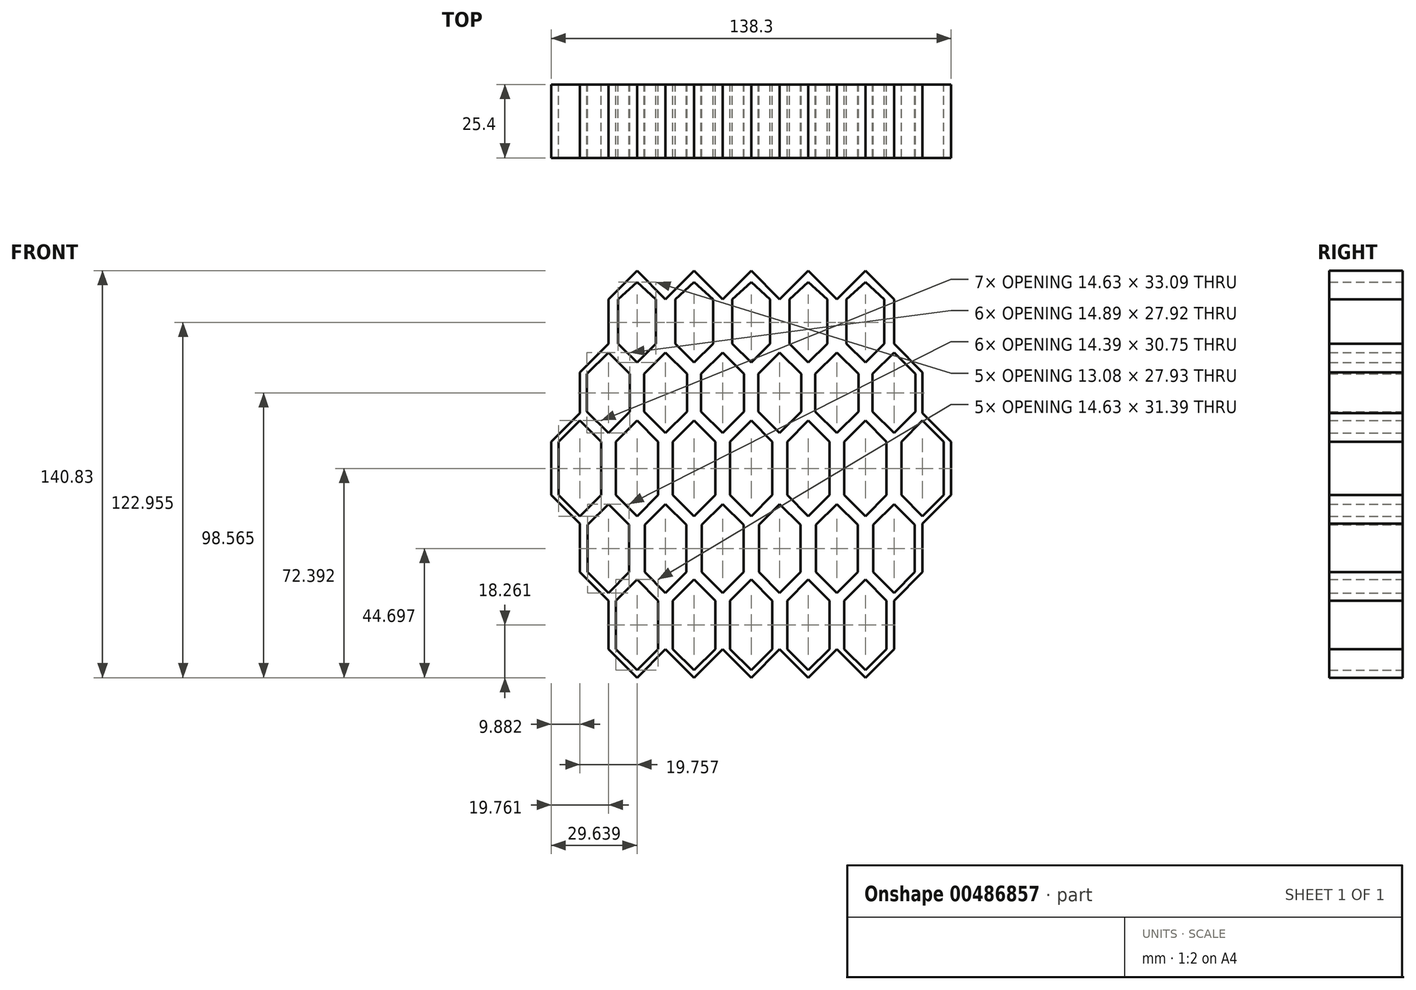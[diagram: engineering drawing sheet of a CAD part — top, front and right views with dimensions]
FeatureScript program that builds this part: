
annotation { "Feature Type Name" : "Feature", "Feature Type Description" : "" }
export const myFeature = defineFeature(function(context is Context, id is Id, definition is map)
    precondition{}
    {
        {
            var Q0;
            Q0=qCreatedBy(makeId("Front.planeOp"),FACE);
            var sketch = newSketch(context, id + "F0", { "sketchPlane" : qUnion([Q0])});
            skLineSegment(sketch, "E0", {"start": v(-42.67, 59.2) * mm, "end": v(-52.55, 49.33) * mm});
            skLineSegment(sketch, "E1", {"start": v(-52.55, 49.33) * mm, "end": v(-52.55, 33.9) * mm});
            skLineSegment(sketch, "E2", {"start": v(-52.55, 33.9) * mm, "end": v(-42.67, 24.03) * mm});
            skLineSegment(sketch, "E3", {"start": v(-42.67, 24.03) * mm, "end": v(-32.8, 33.9) * mm});
            skLineSegment(sketch, "E4", {"start": v(-32.8, 33.9) * mm, "end": v(-32.8, 49.33) * mm});
            skLineSegment(sketch, "E5", {"start": v(-32.8, 49.33) * mm, "end": v(-42.67, 59.2) * mm});
            skLineSegment(sketch, "E6", {"start": v(-32.8, 49.33) * mm, "end": v(-22.91, 59.2) * mm});
            skLineSegment(sketch, "E7", {"start": v(-22.91, 59.2) * mm, "end": v(-13.04, 49.33) * mm});
            skLineSegment(sketch, "E8", {"start": v(-13.04, 49.33) * mm, "end": v(-13.04, 33.9) * mm});
            skLineSegment(sketch, "E9", {"start": v(-13.04, 33.9) * mm, "end": v(-22.91, 24.03) * mm});
            skLineSegment(sketch, "E10", {"start": v(-22.91, 24.03) * mm, "end": v(-32.8, 33.9) * mm});
            skLineSegment(sketch, "E11", {"start": v(-13.04, 49.33) * mm, "end": v(-3.16, 59.2) * mm});
            skLineSegment(sketch, "E12", {"start": v(-3.16, 59.2) * mm, "end": v(6.72, 49.33) * mm});
            skLineSegment(sketch, "E13", {"start": v(6.72, 49.33) * mm, "end": v(6.72, 33.9) * mm});
            skLineSegment(sketch, "E14", {"start": v(6.72, 33.9) * mm, "end": v(-3.16, 24.03) * mm});
            skLineSegment(sketch, "E15", {"start": v(-3.16, 24.03) * mm, "end": v(-13.04, 33.9) * mm});
            skLineSegment(sketch, "E16", {"start": v(6.72, 49.33) * mm, "end": v(16.6, 59.2) * mm});
            skLineSegment(sketch, "E17", {"start": v(16.6, 59.2) * mm, "end": v(26.48, 49.33) * mm});
            skLineSegment(sketch, "E18", {"start": v(26.48, 49.33) * mm, "end": v(26.48, 33.9) * mm});
            skLineSegment(sketch, "E19", {"start": v(26.48, 33.9) * mm, "end": v(16.6, 24.03) * mm});
            skLineSegment(sketch, "E20", {"start": v(16.6, 24.03) * mm, "end": v(6.72, 33.9) * mm});
            skLineSegment(sketch, "E21", {"start": v(26.48, 49.33) * mm, "end": v(36.36, 59.2) * mm});
            skLineSegment(sketch, "E22", {"start": v(36.36, 59.2) * mm, "end": v(46.23, 49.33) * mm});
            skLineSegment(sketch, "E23", {"start": v(46.23, 49.33) * mm, "end": v(46.23, 33.9) * mm});
            skLineSegment(sketch, "E24", {"start": v(46.23, 33.9) * mm, "end": v(36.36, 24.03) * mm});
            skLineSegment(sketch, "E25", {"start": v(36.36, 24.03) * mm, "end": v(26.48, 33.9) * mm});
            skLineSegment(sketch, "E26", {"start": v(-42.67, 24.03) * mm, "end": v(-42.67, 9.88) * mm});
            skLineSegment(sketch, "E27", {"start": v(-42.67, 9.88) * mm, "end": v(-32.8, 0) * mm});
            skLineSegment(sketch, "E28", {"start": v(-32.8, 0) * mm, "end": v(-22.91, 9.88) * mm});
            skLineSegment(sketch, "E29", {"start": v(-22.91, 9.88) * mm, "end": v(-22.91, 24.03) * mm});
            skLineSegment(sketch, "E30", {"start": v(-3.16, 24.03) * mm, "end": v(-3.16, 9.88) * mm});
            skLineSegment(sketch, "E31", {"start": v(-3.16, 9.88) * mm, "end": v(-13.04, 0) * mm});
            skLineSegment(sketch, "E32", {"start": v(-13.04, 0) * mm, "end": v(-22.91, 9.88) * mm});
            skLineSegment(sketch, "E33", {"start": v(16.6, 24.03) * mm, "end": v(16.6, 9.88) * mm});
            skLineSegment(sketch, "E34", {"start": v(-3.16, 9.88) * mm, "end": v(6.72, 0) * mm});
            skLineSegment(sketch, "E35", {"start": v(6.72, 0) * mm, "end": v(16.6, 9.88) * mm});
            skLineSegment(sketch, "E36", {"start": v(16.6, 9.88) * mm, "end": v(26.48, 0) * mm});
            skLineSegment(sketch, "E37", {"start": v(26.48, 0) * mm, "end": v(36.36, 9.88) * mm});
            skLineSegment(sketch, "E38", {"start": v(36.36, 9.88) * mm, "end": v(36.36, 24.03) * mm});
            skLineSegment(sketch, "E39", {"start": v(46.23, 33.9) * mm, "end": v(56.11, 24.03) * mm});
            skLineSegment(sketch, "E40", {"start": v(56.11, 24.03) * mm, "end": v(56.11, 9.88) * mm});
            skLineSegment(sketch, "E41", {"start": v(56.11, 9.88) * mm, "end": v(46.23, 0) * mm});
            skLineSegment(sketch, "E42", {"start": v(46.23, 0) * mm, "end": v(36.36, 9.88) * mm});
            skLineSegment(sketch, "E43", {"start": v(-52.55, 33.9) * mm, "end": v(-62.43, 24.03) * mm});
            skLineSegment(sketch, "E44", {"start": v(-62.43, 24.03) * mm, "end": v(-62.43, 9.88) * mm});
            skLineSegment(sketch, "E45", {"start": v(-62.43, 9.88) * mm, "end": v(-52.55, 0) * mm});
            skLineSegment(sketch, "E46", {"start": v(-52.55, 0) * mm, "end": v(-42.67, 9.88) * mm});
            skLineSegment(sketch, "E47", {"start": v(-62.43, 9.88) * mm, "end": v(-72.3, 0) * mm});
            skLineSegment(sketch, "E48", {"start": v(-72.3, 0) * mm, "end": v(-72.3, -18.46) * mm});
            skLineSegment(sketch, "E49", {"start": v(-52.55, 0) * mm, "end": v(-52.55, -18.46) * mm});
            skLineSegment(sketch, "E50", {"start": v(-52.55, -18.46) * mm, "end": v(-62.43, -28.34) * mm});
            skLineSegment(sketch, "E51", {"start": v(-62.43, -28.34) * mm, "end": v(-72.3, -18.46) * mm});
            skLineSegment(sketch, "E52", {"start": v(-32.8, 0) * mm, "end": v(-32.8, -18.46) * mm});
            skLineSegment(sketch, "E53", {"start": v(-32.8, -18.46) * mm, "end": v(-42.67, -28.34) * mm});
            skLineSegment(sketch, "E54", {"start": v(-42.67, -28.34) * mm, "end": v(-52.55, -18.46) * mm});
            skLineSegment(sketch, "E55", {"start": v(-13.04, 0) * mm, "end": v(-13.04, -18.46) * mm});
            skLineSegment(sketch, "E56", {"start": v(-13.04, -18.46) * mm, "end": v(-22.91, -28.34) * mm});
            skLineSegment(sketch, "E57", {"start": v(-22.91, -28.34) * mm, "end": v(-32.8, -18.46) * mm});
            skLineSegment(sketch, "E58", {"start": v(6.72, 0) * mm, "end": v(6.72, -18.46) * mm});
            skLineSegment(sketch, "E59", {"start": v(6.72, -18.46) * mm, "end": v(-3.16, -28.34) * mm});
            skLineSegment(sketch, "E60", {"start": v(-3.16, -28.34) * mm, "end": v(-13.04, -18.46) * mm});
            skLineSegment(sketch, "E61", {"start": v(26.48, 0) * mm, "end": v(26.48, -18.46) * mm});
            skLineSegment(sketch, "E62", {"start": v(26.48, -18.46) * mm, "end": v(16.6, -28.34) * mm});
            skLineSegment(sketch, "E63", {"start": v(16.6, -28.34) * mm, "end": v(6.72, -18.46) * mm});
            skLineSegment(sketch, "E64", {"start": v(46.23, 0) * mm, "end": v(46.23, -18.46) * mm});
            skLineSegment(sketch, "E65", {"start": v(46.23, -18.46) * mm, "end": v(36.36, -28.34) * mm});
            skLineSegment(sketch, "E66", {"start": v(36.36, -28.34) * mm, "end": v(26.48, -18.46) * mm});
            skLineSegment(sketch, "E67", {"start": v(56.11, 9.88) * mm, "end": v(65.99, 0) * mm});
            skLineSegment(sketch, "E68", {"start": v(65.99, 0) * mm, "end": v(65.99, -18.46) * mm});
            skLineSegment(sketch, "E69", {"start": v(65.99, -18.46) * mm, "end": v(56.11, -28.34) * mm});
            skLineSegment(sketch, "E70", {"start": v(56.11, -28.34) * mm, "end": v(46.23, -18.46) * mm});
            skLineSegment(sketch, "E71", {"start": v(-62.43, -28.34) * mm, "end": v(-62.43, -45.1) * mm});
            skLineSegment(sketch, "E72", {"start": v(-42.67, -28.34) * mm, "end": v(-42.67, -45.1) * mm});
            skLineSegment(sketch, "E73", {"start": v(-42.67, -45.1) * mm, "end": v(-52.55, -54.98) * mm});
            skLineSegment(sketch, "E74", {"start": v(-52.55, -54.98) * mm, "end": v(-62.43, -45.1) * mm});
            skLineSegment(sketch, "E75", {"start": v(-22.91, -28.34) * mm, "end": v(-22.91, -45.1) * mm});
            skLineSegment(sketch, "E76", {"start": v(-22.91, -45.1) * mm, "end": v(-32.8, -54.98) * mm});
            skLineSegment(sketch, "E77", {"start": v(-32.8, -54.98) * mm, "end": v(-42.67, -45.1) * mm});
            skLineSegment(sketch, "E78", {"start": v(-3.16, -28.34) * mm, "end": v(-3.16, -45.1) * mm});
            skLineSegment(sketch, "E79", {"start": v(-3.16, -45.1) * mm, "end": v(-13.04, -54.98) * mm});
            skLineSegment(sketch, "E80", {"start": v(-13.04, -54.98) * mm, "end": v(-22.91, -45.1) * mm});
            skLineSegment(sketch, "E81", {"start": v(16.6, -28.34) * mm, "end": v(16.6, -45.1) * mm});
            skLineSegment(sketch, "E82", {"start": v(16.6, -45.1) * mm, "end": v(6.72, -54.98) * mm});
            skLineSegment(sketch, "E83", {"start": v(6.72, -54.98) * mm, "end": v(-3.16, -45.1) * mm});
            skLineSegment(sketch, "E84", {"start": v(36.36, -28.34) * mm, "end": v(36.36, -45.1) * mm});
            skLineSegment(sketch, "E85", {"start": v(36.36, -45.1) * mm, "end": v(26.48, -54.98) * mm});
            skLineSegment(sketch, "E86", {"start": v(26.48, -54.98) * mm, "end": v(16.6, -45.1) * mm});
            skLineSegment(sketch, "E87", {"start": v(56.11, -28.34) * mm, "end": v(56.11, -45.1) * mm});
            skLineSegment(sketch, "E88", {"start": v(56.11, -45.1) * mm, "end": v(46.23, -54.98) * mm});
            skLineSegment(sketch, "E89", {"start": v(46.23, -54.98) * mm, "end": v(36.36, -45.1) * mm});
            skLineSegment(sketch, "E90", {"start": v(-52.55, -54.98) * mm, "end": v(-52.55, -71.74) * mm});
            skLineSegment(sketch, "E91", {"start": v(-32.8, -54.98) * mm, "end": v(-32.8, -71.74) * mm});
            skLineSegment(sketch, "E92", {"start": v(-13.04, -54.98) * mm, "end": v(-13.04, -71.74) * mm});
            skLineSegment(sketch, "E93", {"start": v(-13.04, -71.74) * mm, "end": v(-22.91, -81.62) * mm});
            skLineSegment(sketch, "E94", {"start": v(-22.91, -81.62) * mm, "end": v(-32.8, -71.74) * mm});
            skLineSegment(sketch, "E95", {"start": v(-52.55, -71.74) * mm, "end": v(-42.67, -81.62) * mm});
            skLineSegment(sketch, "E96", {"start": v(-42.67, -81.62) * mm, "end": v(-32.8, -71.74) * mm});
            skLineSegment(sketch, "E97", {"start": v(6.72, -54.98) * mm, "end": v(6.72, -71.74) * mm});
            skLineSegment(sketch, "E98", {"start": v(6.72, -71.74) * mm, "end": v(-3.16, -81.62) * mm});
            skLineSegment(sketch, "E99", {"start": v(-3.16, -81.62) * mm, "end": v(-13.04, -71.74) * mm});
            skLineSegment(sketch, "E100", {"start": v(26.48, -54.98) * mm, "end": v(26.48, -71.74) * mm});
            skLineSegment(sketch, "E101", {"start": v(26.48, -71.74) * mm, "end": v(16.6, -81.62) * mm});
            skLineSegment(sketch, "E102", {"start": v(16.6, -81.62) * mm, "end": v(6.72, -71.74) * mm});
            skLineSegment(sketch, "E103", {"start": v(46.23, -54.98) * mm, "end": v(46.23, -71.74) * mm});
            skLineSegment(sketch, "E104", {"start": v(46.23, -71.74) * mm, "end": v(36.36, -81.62) * mm});
            skLineSegment(sketch, "E105", {"start": v(36.36, -81.62) * mm, "end": v(26.48, -71.74) * mm});
            skLineSegment(sketch, "E106", {"start": v(-49.21, 49.33) * mm, "end": v(-49.21, 33.9) * mm});
            skLineSegment(sketch, "E107", {"start": v(-49.21, 33.9) * mm, "end": v(-42.67, 27.37) * mm});
            skPoint(sketch, "E107.endSnap0", {"position": v(-42.67, 16.95) * mm});
            skLineSegment(sketch, "E108", {"start": v(-42.67, 55.3) * mm, "end": v(-49.21, 49.33) * mm});
            skLineSegment(sketch, "E109.MirrorCS", {"start": v(-42.67, 55.3) * mm, "end": v(-36.13, 49.33) * mm});
            skLineSegment(sketch, "E110.MirrorCS", {"start": v(-36.13, 49.33) * mm, "end": v(-36.13, 33.9) * mm});
            skLineSegment(sketch, "E111.MirrorCS", {"start": v(-36.13, 33.9) * mm, "end": v(-42.67, 27.37) * mm});
            skLineSegment(sketch, "E112.MirrorCS", {"start": v(-29.46, 49.33) * mm, "end": v(-29.46, 33.9) * mm});
            skLineSegment(sketch, "E113.MirrorCS", {"start": v(-22.91, 55.3) * mm, "end": v(-29.46, 49.33) * mm});
            skLineSegment(sketch, "E114.MirrorCS", {"start": v(-22.91, 55.3) * mm, "end": v(-16.37, 49.33) * mm});
            skLineSegment(sketch, "E115.MirrorCS", {"start": v(-16.37, 49.33) * mm, "end": v(-16.37, 33.9) * mm});
            skLineSegment(sketch, "E116.MirrorCS", {"start": v(-16.37, 33.9) * mm, "end": v(-22.91, 27.37) * mm});
            skLineSegment(sketch, "E117.MirrorCS", {"start": v(-29.46, 33.9) * mm, "end": v(-22.91, 27.37) * mm});
            skLineSegment(sketch, "E118.MirrorCS", {"start": v(-9.7, 49.33) * mm, "end": v(-9.7, 33.9) * mm});
            skLineSegment(sketch, "E119.MirrorCS", {"start": v(3.38, 49.33) * mm, "end": v(3.38, 33.9) * mm});
            skLineSegment(sketch, "E120.MirrorCS", {"start": v(-3.16, 55.3) * mm, "end": v(3.38, 49.33) * mm});
            skLineSegment(sketch, "E121.MirrorCS", {"start": v(-3.16, 55.3) * mm, "end": v(-9.7, 49.33) * mm});
            skLineSegment(sketch, "E122.MirrorCS", {"start": v(3.38, 33.9) * mm, "end": v(-3.16, 27.37) * mm});
            skLineSegment(sketch, "E123.MirrorCS", {"start": v(-9.7, 33.9) * mm, "end": v(-3.16, 27.37) * mm});
            skLineSegment(sketch, "E124.MirrorCS", {"start": v(10.06, 49.33) * mm, "end": v(10.06, 33.9) * mm});
            skLineSegment(sketch, "E125.MirrorCS", {"start": v(16.6, 55.3) * mm, "end": v(10.06, 49.33) * mm});
            skLineSegment(sketch, "E126.MirrorCS", {"start": v(16.6, 55.3) * mm, "end": v(23.14, 49.33) * mm});
            skLineSegment(sketch, "E127.MirrorCS", {"start": v(23.14, 49.33) * mm, "end": v(23.14, 33.9) * mm});
            skLineSegment(sketch, "E128.MirrorCS", {"start": v(23.14, 33.9) * mm, "end": v(16.6, 27.37) * mm});
            skLineSegment(sketch, "E129.MirrorCS", {"start": v(10.06, 33.9) * mm, "end": v(16.6, 27.37) * mm});
            skLineSegment(sketch, "E130.MirrorCS", {"start": v(29.81, 49.33) * mm, "end": v(29.81, 33.9) * mm});
            skLineSegment(sketch, "E131.MirrorCS", {"start": v(42.9, 49.33) * mm, "end": v(42.9, 33.9) * mm});
            skLineSegment(sketch, "E132.MirrorCS", {"start": v(36.36, 55.3) * mm, "end": v(42.9, 49.33) * mm});
            skLineSegment(sketch, "E133.MirrorCS", {"start": v(36.36, 55.3) * mm, "end": v(29.81, 49.33) * mm});
            skLineSegment(sketch, "E134.MirrorCS", {"start": v(29.81, 33.9) * mm, "end": v(36.36, 27.37) * mm});
            skLineSegment(sketch, "E135.MirrorCS", {"start": v(42.9, 33.9) * mm, "end": v(36.36, 27.37) * mm});
            skLineSegment(sketch, "E136", {"start": v(-40.24, 23.46) * mm, "end": v(-40.24, 10.43) * mm});
            skLineSegment(sketch, "E137", {"start": v(-40.24, 10.43) * mm, "end": v(-32.8, 2.99) * mm});
            skLineSegment(sketch, "E138", {"start": v(-40.24, 23.46) * mm, "end": v(-32.8, 30.9) * mm});
            skLineSegment(sketch, "E139.MirrorCS", {"start": v(-25.35, 23.46) * mm, "end": v(-32.8, 30.9) * mm});
            skPoint(sketch, "E140.MirrorP", {"position": v(-22.91, 16.95) * mm});
            skLineSegment(sketch, "E141.MirrorCS", {"start": v(-25.35, 10.43) * mm, "end": v(-32.8, 2.99) * mm});
            skLineSegment(sketch, "E142.MirrorCS", {"start": v(-25.35, 23.46) * mm, "end": v(-25.35, 10.43) * mm});
            skLineSegment(sketch, "E143.MirrorCS", {"start": v(-45.1, 23.46) * mm, "end": v(-52.55, 30.9) * mm});
            skLineSegment(sketch, "E144.MirrorCS", {"start": v(-60, 23.46) * mm, "end": v(-52.55, 30.9) * mm});
            skPoint(sketch, "E145.MirrorP", {"position": v(-62.43, 16.95) * mm});
            skLineSegment(sketch, "E146.MirrorCS", {"start": v(-60, 23.46) * mm, "end": v(-60, 10.43) * mm});
            skLineSegment(sketch, "E147.MirrorCS", {"start": v(-60, 10.43) * mm, "end": v(-52.55, 2.99) * mm});
            skLineSegment(sketch, "E148.MirrorCS", {"start": v(-45.1, 10.43) * mm, "end": v(-52.55, 2.99) * mm});
            skLineSegment(sketch, "E149.MirrorCS", {"start": v(-45.1, 23.46) * mm, "end": v(-45.1, 10.43) * mm});
            skLineSegment(sketch, "E150.MirrorCS", {"start": v(-20.48, 23.46) * mm, "end": v(-20.48, 10.43) * mm});
            skLineSegment(sketch, "E151.MirrorCS", {"start": v(-5.6, 23.46) * mm, "end": v(-5.6, 10.43) * mm});
            skLineSegment(sketch, "E152.MirrorCS", {"start": v(-5.6, 23.46) * mm, "end": v(-13.04, 30.9) * mm});
            skLineSegment(sketch, "E153.MirrorCS", {"start": v(-20.48, 23.46) * mm, "end": v(-13.04, 30.9) * mm});
            skLineSegment(sketch, "E154.MirrorCS", {"start": v(-20.48, 10.43) * mm, "end": v(-13.04, 2.99) * mm});
            skLineSegment(sketch, "E155.MirrorCS", {"start": v(-5.6, 10.43) * mm, "end": v(-13.04, 2.99) * mm});
            skLineSegment(sketch, "E156.MirrorCS", {"start": v(-0.72, 23.46) * mm, "end": v(-0.72, 10.43) * mm});
            skLineSegment(sketch, "E157.MirrorCS", {"start": v(14.17, 23.46) * mm, "end": v(14.17, 10.43) * mm});
            skLineSegment(sketch, "E158.MirrorCS", {"start": v(14.17, 23.46) * mm, "end": v(6.72, 30.9) * mm});
            skLineSegment(sketch, "E159.MirrorCS", {"start": v(-0.72, 23.46) * mm, "end": v(6.72, 30.9) * mm});
            skLineSegment(sketch, "E160.MirrorCS", {"start": v(-0.72, 10.43) * mm, "end": v(6.72, 2.99) * mm});
            skLineSegment(sketch, "E161.MirrorCS", {"start": v(14.17, 10.43) * mm, "end": v(6.72, 2.99) * mm});
            skLineSegment(sketch, "E162.MirrorCS", {"start": v(19.03, 23.46) * mm, "end": v(19.03, 10.43) * mm});
            skLineSegment(sketch, "E163.MirrorCS", {"start": v(33.92, 23.46) * mm, "end": v(33.92, 10.43) * mm});
            skLineSegment(sketch, "E164.MirrorCS", {"start": v(33.92, 23.46) * mm, "end": v(26.48, 30.9) * mm});
            skLineSegment(sketch, "E165.MirrorCS", {"start": v(19.03, 23.46) * mm, "end": v(26.48, 30.9) * mm});
            skLineSegment(sketch, "E166.MirrorCS", {"start": v(19.03, 10.43) * mm, "end": v(26.48, 2.99) * mm});
            skLineSegment(sketch, "E167.MirrorCS", {"start": v(33.92, 10.43) * mm, "end": v(26.48, 2.99) * mm});
            skLineSegment(sketch, "E168.MirrorCS", {"start": v(38.79, 23.46) * mm, "end": v(38.79, 10.43) * mm});
            skLineSegment(sketch, "E169.MirrorCS", {"start": v(53.68, 23.46) * mm, "end": v(53.68, 10.43) * mm});
            skLineSegment(sketch, "E170.MirrorCS", {"start": v(53.68, 23.46) * mm, "end": v(46.23, 30.9) * mm});
            skLineSegment(sketch, "E171.MirrorCS", {"start": v(38.79, 23.46) * mm, "end": v(46.23, 30.9) * mm});
            skLineSegment(sketch, "E172.MirrorCS", {"start": v(38.79, 10.43) * mm, "end": v(46.23, 2.99) * mm});
            skLineSegment(sketch, "E173.MirrorCS", {"start": v(53.68, 10.43) * mm, "end": v(46.23, 2.99) * mm});
            skLineSegment(sketch, "E174", {"start": v(-49.99, 0) * mm, "end": v(-49.99, -18.46) * mm});
            skLineSegment(sketch, "E175", {"start": v(-49.99, -18.46) * mm, "end": v(-42.67, -25.77) * mm});
            skLineSegment(sketch, "E176", {"start": v(-49.99, 0) * mm, "end": v(-42.67, 7.31) * mm});
            skLineSegment(sketch, "E177.MirrorCS", {"start": v(-35.36, 0) * mm, "end": v(-42.67, 7.31) * mm});
            skLineSegment(sketch, "E178.MirrorCS", {"start": v(-35.36, 0) * mm, "end": v(-35.36, -18.46) * mm});
            skLineSegment(sketch, "E179.MirrorCS", {"start": v(-35.36, -18.46) * mm, "end": v(-42.67, -25.77) * mm});
            skLineSegment(sketch, "E180.MirrorCS", {"start": v(-55.11, 0) * mm, "end": v(-55.11, -18.46) * mm});
            skLineSegment(sketch, "E181.MirrorCS", {"start": v(-69.74, 0) * mm, "end": v(-62.43, 7.31) * mm});
            skLineSegment(sketch, "E182.MirrorCS", {"start": v(-55.11, 0) * mm, "end": v(-62.43, 7.31) * mm});
            skLineSegment(sketch, "E183.MirrorCS", {"start": v(-69.74, 0) * mm, "end": v(-69.74, -18.46) * mm});
            skLineSegment(sketch, "E184.MirrorCS", {"start": v(-69.74, -18.46) * mm, "end": v(-62.43, -25.77) * mm});
            skLineSegment(sketch, "E185.MirrorCS", {"start": v(-55.11, -18.46) * mm, "end": v(-62.43, -25.77) * mm});
            skLineSegment(sketch, "E186.MirrorCS", {"start": v(-30.23, 0) * mm, "end": v(-30.23, -18.46) * mm});
            skLineSegment(sketch, "E187.MirrorCS", {"start": v(-15.6, 0) * mm, "end": v(-15.6, -18.46) * mm});
            skLineSegment(sketch, "E188.MirrorCS", {"start": v(-15.6, 0) * mm, "end": v(-22.91, 7.31) * mm});
            skLineSegment(sketch, "E189.MirrorCS", {"start": v(-30.23, 0) * mm, "end": v(-22.91, 7.31) * mm});
            skLineSegment(sketch, "E190.MirrorCS", {"start": v(-30.23, -18.46) * mm, "end": v(-22.91, -25.77) * mm});
            skLineSegment(sketch, "E191.MirrorCS", {"start": v(-15.6, -18.46) * mm, "end": v(-22.91, -25.77) * mm});
            skLineSegment(sketch, "E192.MirrorCS", {"start": v(-10.47, 0) * mm, "end": v(-10.47, -18.46) * mm});
            skLineSegment(sketch, "E193.MirrorCS", {"start": v(-10.47, 0) * mm, "end": v(-3.16, 7.31) * mm});
            skLineSegment(sketch, "E194.MirrorCS", {"start": v(4.16, 0) * mm, "end": v(-3.16, 7.31) * mm});
            skLineSegment(sketch, "E195.MirrorCS", {"start": v(4.16, 0) * mm, "end": v(4.16, -18.46) * mm});
            skLineSegment(sketch, "E196.MirrorCS", {"start": v(4.16, -18.46) * mm, "end": v(-3.16, -25.77) * mm});
            skLineSegment(sketch, "E197.MirrorCS", {"start": v(-10.47, -18.46) * mm, "end": v(-3.16, -25.77) * mm});
            skLineSegment(sketch, "E198.MirrorCS", {"start": v(9.28, 0) * mm, "end": v(9.28, -18.46) * mm});
            skLineSegment(sketch, "E199.MirrorCS", {"start": v(23.91, 0) * mm, "end": v(23.91, -18.46) * mm});
            skLineSegment(sketch, "E200.MirrorCS", {"start": v(23.91, 0) * mm, "end": v(16.6, 7.31) * mm});
            skLineSegment(sketch, "E201.MirrorCS", {"start": v(9.28, 0) * mm, "end": v(16.6, 7.31) * mm});
            skLineSegment(sketch, "E202.MirrorCS", {"start": v(9.28, -18.46) * mm, "end": v(16.6, -25.77) * mm});
            skLineSegment(sketch, "E203.MirrorCS", {"start": v(23.91, -18.46) * mm, "end": v(16.6, -25.77) * mm});
            skLineSegment(sketch, "E204.MirrorCS", {"start": v(29.04, 0) * mm, "end": v(29.04, -18.46) * mm});
            skLineSegment(sketch, "E205.MirrorCS", {"start": v(43.67, 0) * mm, "end": v(43.67, -18.46) * mm});
            skLineSegment(sketch, "E206.MirrorCS", {"start": v(43.67, 0) * mm, "end": v(36.36, 7.31) * mm});
            skLineSegment(sketch, "E207.MirrorCS", {"start": v(29.04, 0) * mm, "end": v(36.36, 7.31) * mm});
            skLineSegment(sketch, "E208.MirrorCS", {"start": v(29.04, -18.46) * mm, "end": v(36.36, -25.77) * mm});
            skLineSegment(sketch, "E209.MirrorCS", {"start": v(43.67, -18.46) * mm, "end": v(36.36, -25.77) * mm});
            skLineSegment(sketch, "E210.MirrorCS", {"start": v(36.36, 9.88) * mm, "end": v(46.23, 0) * mm});
            skLineSegment(sketch, "E211.MirrorCS", {"start": v(36.36, 9.88) * mm, "end": v(26.48, 0) * mm});
            skLineSegment(sketch, "E212.MirrorCS", {"start": v(26.48, -18.46) * mm, "end": v(36.36, -28.34) * mm});
            skLineSegment(sketch, "E213.MirrorCS", {"start": v(48.8, 0) * mm, "end": v(48.8, -18.46) * mm});
            skLineSegment(sketch, "E214.MirrorCS", {"start": v(48.8, 0) * mm, "end": v(56.11, 7.31) * mm});
            skLineSegment(sketch, "E215.MirrorCS", {"start": v(63.43, 0) * mm, "end": v(56.11, 7.31) * mm});
            skLineSegment(sketch, "E216.MirrorCS", {"start": v(63.43, 0) * mm, "end": v(63.43, -18.46) * mm});
            skLineSegment(sketch, "E217.MirrorCS", {"start": v(63.43, -18.46) * mm, "end": v(56.11, -25.77) * mm});
            skLineSegment(sketch, "E218.MirrorCS", {"start": v(48.8, -18.46) * mm, "end": v(56.11, -25.77) * mm});
            skLineSegment(sketch, "E219", {"start": v(-59.75, -28.75) * mm, "end": v(-59.75, -45.1) * mm});
            skLineSegment(sketch, "E220", {"start": v(-59.75, -45.1) * mm, "end": v(-52.55, -52.3) * mm});
            skLineSegment(sketch, "E221", {"start": v(-59.75, -28.75) * mm, "end": v(-52.55, -21.55) * mm});
            skLineSegment(sketch, "E222.MirrorCS", {"start": v(-45.35, -28.75) * mm, "end": v(-52.55, -21.55) * mm});
            skLineSegment(sketch, "E223.MirrorCS", {"start": v(-45.35, -28.75) * mm, "end": v(-45.35, -45.1) * mm});
            skLineSegment(sketch, "E224.MirrorCS", {"start": v(-45.35, -45.1) * mm, "end": v(-52.55, -52.3) * mm});
            skLineSegment(sketch, "E225.MirrorCS", {"start": v(-39.99, -28.75) * mm, "end": v(-39.99, -45.1) * mm});
            skLineSegment(sketch, "E226.MirrorCS", {"start": v(-39.99, -28.75) * mm, "end": v(-32.8, -21.55) * mm});
            skLineSegment(sketch, "E227.MirrorCS", {"start": v(-39.99, -45.1) * mm, "end": v(-32.8, -52.3) * mm});
            skLineSegment(sketch, "E228.MirrorCS", {"start": v(-25.6, -45.1) * mm, "end": v(-32.8, -52.3) * mm});
            skLineSegment(sketch, "E229.MirrorCS", {"start": v(-25.6, -28.75) * mm, "end": v(-25.6, -45.1) * mm});
            skLineSegment(sketch, "E230.MirrorCS", {"start": v(-25.6, -28.75) * mm, "end": v(-32.8, -21.55) * mm});
            skLineSegment(sketch, "E231.MirrorCS", {"start": v(-20.23, -28.75) * mm, "end": v(-20.23, -45.1) * mm});
            skLineSegment(sketch, "E232.MirrorCS", {"start": v(-20.23, -28.75) * mm, "end": v(-13.04, -21.55) * mm});
            skLineSegment(sketch, "E233.MirrorCS", {"start": v(-5.84, -28.75) * mm, "end": v(-13.04, -21.55) * mm});
            skLineSegment(sketch, "E234.MirrorCS", {"start": v(-5.84, -28.75) * mm, "end": v(-5.84, -45.1) * mm});
            skLineSegment(sketch, "E235.MirrorCS", {"start": v(-5.84, -45.1) * mm, "end": v(-13.04, -52.3) * mm});
            skLineSegment(sketch, "E236.MirrorCS", {"start": v(-20.23, -45.1) * mm, "end": v(-13.04, -52.3) * mm});
            skLineSegment(sketch, "E237.MirrorCS", {"start": v(-0.48, -28.75) * mm, "end": v(-0.48, -45.1) * mm});
            skLineSegment(sketch, "E238.MirrorCS", {"start": v(-0.48, -28.75) * mm, "end": v(6.72, -21.55) * mm});
            skLineSegment(sketch, "E239.MirrorCS", {"start": v(13.92, -28.75) * mm, "end": v(6.72, -21.55) * mm});
            skLineSegment(sketch, "E240.MirrorCS", {"start": v(13.92, -28.75) * mm, "end": v(13.92, -45.1) * mm});
            skLineSegment(sketch, "E241.MirrorCS", {"start": v(13.92, -45.1) * mm, "end": v(6.72, -52.3) * mm});
            skLineSegment(sketch, "E242.MirrorCS", {"start": v(-0.48, -45.1) * mm, "end": v(6.72, -52.3) * mm});
            skLineSegment(sketch, "E243.MirrorCS", {"start": v(19.28, -28.75) * mm, "end": v(19.28, -45.1) * mm});
            skLineSegment(sketch, "E244.MirrorCS", {"start": v(19.28, -28.75) * mm, "end": v(26.48, -21.55) * mm});
            skLineSegment(sketch, "E245.MirrorCS", {"start": v(33.67, -28.75) * mm, "end": v(26.48, -21.55) * mm});
            skLineSegment(sketch, "E246.MirrorCS", {"start": v(33.67, -28.75) * mm, "end": v(33.67, -45.1) * mm});
            skLineSegment(sketch, "E247.MirrorCS", {"start": v(33.67, -45.1) * mm, "end": v(26.48, -52.3) * mm});
            skLineSegment(sketch, "E248.MirrorCS", {"start": v(19.28, -45.1) * mm, "end": v(26.48, -52.3) * mm});
            skLineSegment(sketch, "E249.MirrorCS", {"start": v(39.04, -28.75) * mm, "end": v(46.23, -21.55) * mm});
            skLineSegment(sketch, "E250.MirrorCS", {"start": v(39.04, -28.75) * mm, "end": v(39.04, -45.1) * mm});
            skLineSegment(sketch, "E251.MirrorCS", {"start": v(39.04, -45.1) * mm, "end": v(46.23, -52.3) * mm});
            skLineSegment(sketch, "E252.MirrorCS", {"start": v(53.43, -45.1) * mm, "end": v(46.23, -52.3) * mm});
            skLineSegment(sketch, "E253.MirrorCS", {"start": v(53.43, -28.75) * mm, "end": v(53.43, -45.1) * mm});
            skLineSegment(sketch, "E254.MirrorCS", {"start": v(53.43, -28.75) * mm, "end": v(46.23, -21.55) * mm});
            skLineSegment(sketch, "E255", {"start": v(-49.99, -71.74) * mm, "end": v(-42.67, -79.06) * mm});
            skLineSegment(sketch, "E256", {"start": v(-49.99, -54.98) * mm, "end": v(-42.67, -47.66) * mm});
            skLineSegment(sketch, "E257.MirrorCS", {"start": v(-35.36, -54.98) * mm, "end": v(-42.67, -47.66) * mm});
            skLineSegment(sketch, "E258.MirrorCS", {"start": v(-35.36, -54.98) * mm, "end": v(-35.36, -71.74) * mm});
            skLineSegment(sketch, "E259.MirrorCS", {"start": v(-35.36, -71.74) * mm, "end": v(-42.67, -79.06) * mm});
            skLineSegment(sketch, "E260.MirrorCS", {"start": v(-30.23, -54.98) * mm, "end": v(-30.23, -71.74) * mm});
            skLineSegment(sketch, "E261.MirrorCS", {"start": v(-30.23, -54.98) * mm, "end": v(-22.91, -47.66) * mm});
            skLineSegment(sketch, "E262.MirrorCS", {"start": v(-15.6, -54.98) * mm, "end": v(-22.91, -47.66) * mm});
            skLineSegment(sketch, "E263.MirrorCS", {"start": v(-15.6, -54.98) * mm, "end": v(-15.6, -71.74) * mm});
            skLineSegment(sketch, "E264.MirrorCS", {"start": v(-15.6, -71.74) * mm, "end": v(-22.91, -79.06) * mm});
            skLineSegment(sketch, "E265.MirrorCS", {"start": v(-10.47, -54.98) * mm, "end": v(-10.47, -71.74) * mm});
            skLineSegment(sketch, "E266.MirrorCS", {"start": v(-10.47, -54.98) * mm, "end": v(-3.16, -47.66) * mm});
            skLineSegment(sketch, "E267.MirrorCS", {"start": v(4.16, -54.98) * mm, "end": v(-3.16, -47.66) * mm});
            skLineSegment(sketch, "E268.MirrorCS", {"start": v(-30.23, -71.74) * mm, "end": v(-22.91, -79.06) * mm});
            skLineSegment(sketch, "E269.MirrorCS", {"start": v(-10.47, -71.74) * mm, "end": v(-3.16, -79.06) * mm});
            skLineSegment(sketch, "E270.MirrorCS", {"start": v(4.16, -71.74) * mm, "end": v(-3.16, -79.06) * mm});
            skLineSegment(sketch, "E271.MirrorCS", {"start": v(4.16, -54.98) * mm, "end": v(4.16, -71.74) * mm});
            skLineSegment(sketch, "E272.MirrorCS", {"start": v(9.28, -54.98) * mm, "end": v(9.28, -71.74) * mm});
            skLineSegment(sketch, "E273.MirrorCS", {"start": v(9.28, -54.98) * mm, "end": v(16.6, -47.66) * mm});
            skLineSegment(sketch, "E274.MirrorCS", {"start": v(23.91, -54.98) * mm, "end": v(16.6, -47.66) * mm});
            skLineSegment(sketch, "E275.MirrorCS", {"start": v(23.91, -54.98) * mm, "end": v(23.91, -71.74) * mm});
            skLineSegment(sketch, "E276.MirrorCS", {"start": v(23.91, -71.74) * mm, "end": v(16.6, -79.06) * mm});
            skLineSegment(sketch, "E277.MirrorCS", {"start": v(9.28, -71.74) * mm, "end": v(16.6, -79.06) * mm});
            skLineSegment(sketch, "E278.MirrorCS", {"start": v(29.04, -54.98) * mm, "end": v(29.04, -71.74) * mm});
            skLineSegment(sketch, "E279.MirrorCS", {"start": v(29.04, -54.98) * mm, "end": v(36.36, -47.66) * mm});
            skLineSegment(sketch, "E280.MirrorCS", {"start": v(43.67, -54.98) * mm, "end": v(36.36, -47.66) * mm});
            skLineSegment(sketch, "E281.MirrorCS", {"start": v(43.67, -54.98) * mm, "end": v(43.67, -71.74) * mm});
            skLineSegment(sketch, "E282.MirrorCS", {"start": v(43.67, -71.74) * mm, "end": v(36.36, -79.06) * mm});
            skLineSegment(sketch, "E283.MirrorCS", {"start": v(29.04, -71.74) * mm, "end": v(36.36, -79.06) * mm});
            skLineSegment(sketch, "E284", {"start": v(-49.99, -54.98) * mm, "end": v(-49.99, -71.74) * mm});
            skSolve(sketch);
        }
        {
            var Q0;
            Q0=qSketchRegion(id+"F0",true);
            extrude(context, id + "F1", {"entities" : qUnion([Q0]), "depth" : 25.4 * mm});
        }
        {
            var Q0;
            Q0=makeQuery(id+"F0.imprint","IMPRINT",FACE,{"disambiguationData":[TD([[makeQuery(id+"F0.imprint","IMPRINT",EDGE,{"derivedFrom":sQuery(id+"F0.wireOp",EDGE,"E3")}),-1.0]])]});
            var Q1;
            Q1=makeQuery(id+"F0.imprint","IMPRINT",FACE,{"disambiguationData":[TD([[makeQuery(id+"F0.imprint","IMPRINT",EDGE,{"derivedFrom":sQuery(id+"F0.wireOp",EDGE,"E9")}),1.0]])]});
            var Q2;
            Q2=makeQuery(id+"F0.imprint","IMPRINT",FACE,{"disambiguationData":[TD([[makeQuery(id+"F0.imprint","IMPRINT",EDGE,{"derivedFrom":sQuery(id+"F0.wireOp",EDGE,"E28")}),-1.0]])]});
            var Q3;
            Q3=makeQuery(id+"F0.imprint","IMPRINT",FACE,{"disambiguationData":[TD([[makeQuery(id+"F0.imprint","IMPRINT",EDGE,{"derivedFrom":sQuery(id+"F0.wireOp",EDGE,"E31")}),1.0]])]});
            var Q4;
            Q4=makeQuery(id+"F0.imprint","IMPRINT",FACE,{"disambiguationData":[TD([[makeQuery(id+"F0.imprint","IMPRINT",EDGE,{"derivedFrom":sQuery(id+"F0.wireOp",EDGE,"E14")}),1.0]])]});
            var Q5;
            Q5=makeQuery(id+"F0.imprint","IMPRINT",FACE,{"disambiguationData":[TD([[makeQuery(id+"F0.imprint","IMPRINT",EDGE,{"derivedFrom":sQuery(id+"F0.wireOp",EDGE,"E19")}),1.0]])]});
            var Q6;
            Q6=makeQuery(id+"F0.imprint","IMPRINT",FACE,{"disambiguationData":[TD([[makeQuery(id+"F0.imprint","IMPRINT",EDGE,{"derivedFrom":sQuery(id+"F0.wireOp",EDGE,"E64")}),-1.0]])]});
            var Q7;
            Q7=makeQuery(id+"F0.imprint","IMPRINT",FACE,{"disambiguationData":[TD([[makeQuery(id+"F0.imprint","IMPRINT",EDGE,{"derivedFrom":sQuery(id+"F0.wireOp",EDGE,"E35")}),-1.0]])]});
            var Q8;
            Q8=makeQuery(id+"F0.imprint","IMPRINT",FACE,{"disambiguationData":[TD([[makeQuery(id+"F0.imprint","IMPRINT",EDGE,{"derivedFrom":sQuery(id+"F0.wireOp",EDGE,"E59")}),1.0]])]});
            var Q9;
            Q9=makeQuery(id+"F0.imprint","IMPRINT",FACE,{"disambiguationData":[TD([[makeQuery(id+"F0.imprint","IMPRINT",EDGE,{"derivedFrom":sQuery(id+"F0.wireOp",EDGE,"E56")}),1.0]])]});
            var Q10;
            Q10=makeQuery(id+"F0.imprint","IMPRINT",FACE,{"disambiguationData":[TD([[makeQuery(id+"F0.imprint","IMPRINT",EDGE,{"derivedFrom":sQuery(id+"F0.wireOp",EDGE,"E53")}),1.0]])]});
            var Q11;
            Q11=makeQuery(id+"F0.imprint","IMPRINT",FACE,{"disambiguationData":[TD([[makeQuery(id+"F0.imprint","IMPRINT",EDGE,{"derivedFrom":sQuery(id+"F0.wireOp",EDGE,"E27")}),-1.0]])]});
            var Q12;
            Q12=makeQuery(id+"F0.imprint","IMPRINT",FACE,{"disambiguationData":[TD([[makeQuery(id+"F0.imprint","IMPRINT",EDGE,{"derivedFrom":sQuery(id+"F0.wireOp",EDGE,"E62")}),1.0]])]});
            extrude(context, id + "F2", {"entities" : qUnion([Q0, Q1, Q2, Q3, Q4, Q5, Q6, Q7, Q8, Q9, Q10, Q11, Q12]), "operationType" : NewBodyOperationType.ADD, "depth" : 25.4 * mm});
        }
    });
